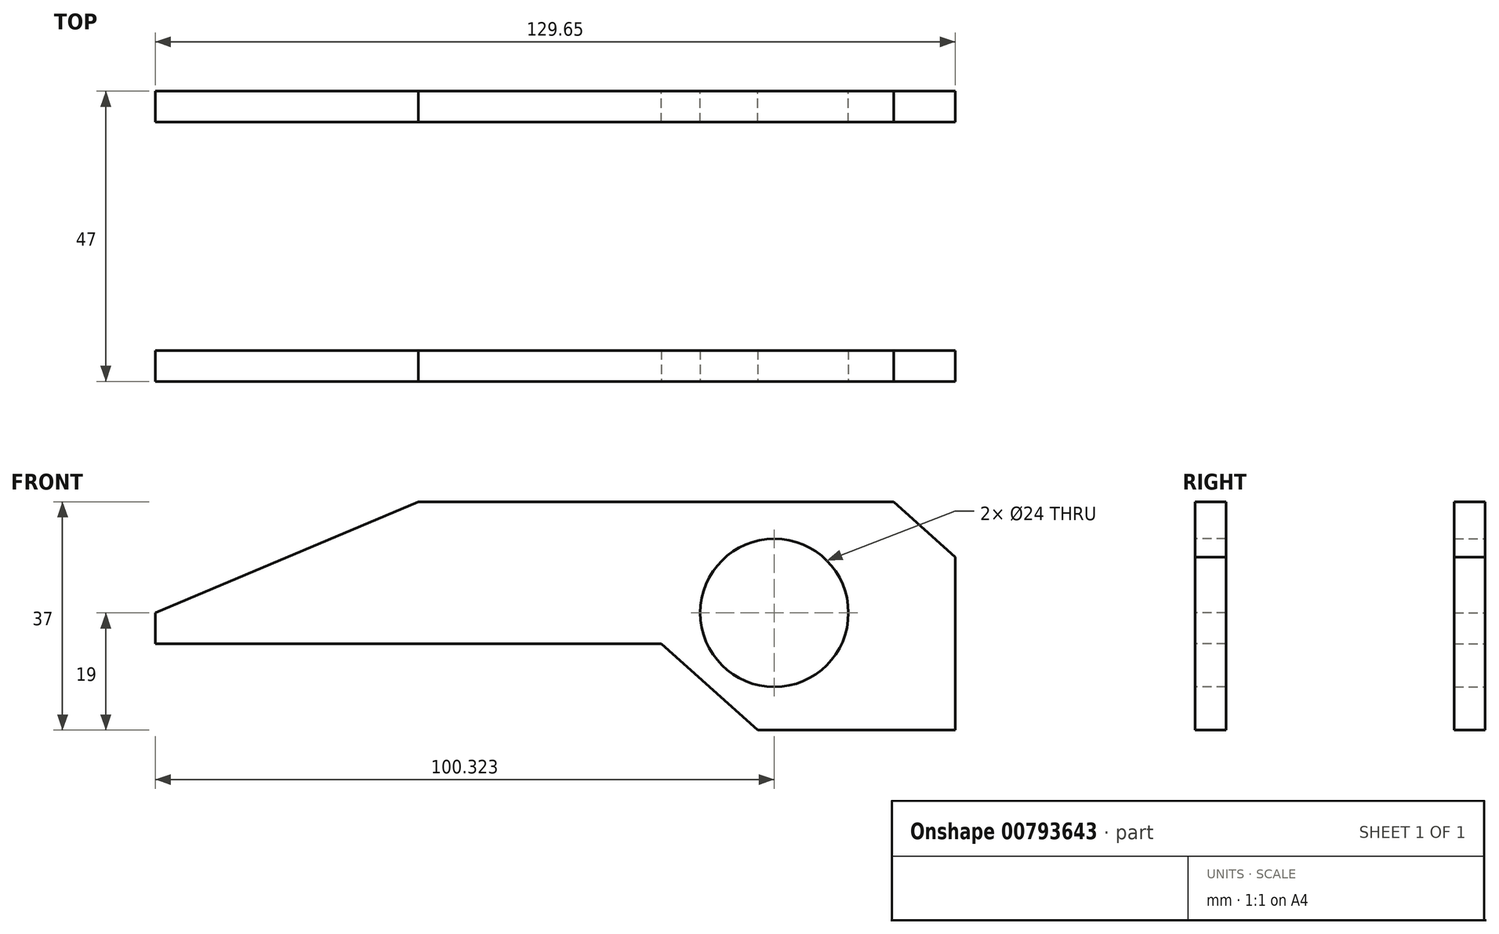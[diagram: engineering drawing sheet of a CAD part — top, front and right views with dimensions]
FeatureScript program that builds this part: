
annotation { "Feature Type Name" : "Feature", "Feature Type Description" : "" }
export const myFeature = defineFeature(function(context is Context, id is Id, definition is map)
    precondition{}
    {
        {
            var Q0;
            Q0=qCreatedBy(makeId("Front.planeOp"),FACE);
            var sketch = newSketch(context, id + "F0", { "sketchPlane" : qUnion([Q0])});
            skLineSegment(sketch, "E0", {"start": v(67.46, 14) * mm, "end": v(57.46, 23) * mm});
            skLineSegment(sketch, "E1", {"start": v(57.46, 23) * mm, "end": v(-19.54, 23) * mm});
            skLineSegment(sketch, "E2", {"start": v(-19.54, 23) * mm, "end": v(-62.2, 5) * mm});
            skLineSegment(sketch, "E3", {"start": v(-62.2, 5) * mm, "end": v(-62.2, 0) * mm});
            skLineSegment(sketch, "E4", {"start": v(-62.2, 0) * mm, "end": v(19.8, 0) * mm});
            skLineSegment(sketch, "E5", {"start": v(19.8, 0) * mm, "end": v(35.46, -14) * mm});
            skLineSegment(sketch, "E6", {"start": v(35.46, -14) * mm, "end": v(67.46, -14) * mm});
            skLineSegment(sketch, "E7", {"start": v(67.46, -14) * mm, "end": v(67.46, 14) * mm});
            skCircle(sketch, "E8", {"center": v(38.13, 5) * mm, "radius": 12 * mm});
            skSolve(sketch);
        }
        {
            var Q0;
            Q0 = qSketchRegion(id + "F0", true);
            extrude(context, id + "F1", {"entities" : qUnion([Q0]), "depth" : 5 * mm, "offsetDistance" : 25 * mm});
        }
        {
            var Q0;
            Q0=qCreatedBy(makeId("Front.planeOp"),FACE);
            cPlane(context, id + "F2", {"entities" : qUnion([Q0]), "cplaneType" : CPlaneType.OFFSET, "offset" : (47 / 2) * mm, "width" : 150 * mm, "height" : 150 * mm});
        }
        {
            var Q0;
            Q0=makeQuery(id+"F1.opExtrude","SWEPT_BODY",BODY,{"disambiguationData":[OSD([sQuery(id+"F0.wireOp",EDGE,"E0"),sQuery(id+"F0.wireOp",EDGE,"E1"),sQuery(id+"F0.wireOp",EDGE,"E2"),sQuery(id+"F0.wireOp",EDGE,"E3"),sQuery(id+"F0.wireOp",EDGE,"E4"),sQuery(id+"F0.wireOp",EDGE,"E5"),sQuery(id+"F0.wireOp",EDGE,"E6"),sQuery(id+"F0.wireOp",EDGE,"E7"),sQuery(id+"F0.wireOp",EDGE,"E8")])]});
            var Q1;
            Q1=qCreatedBy(id+"F2.planeOp",FACE);
            mirror(context, id + "F3", {"operationType" : NewBodyOperationType.ADD, "entities" : qUnion([Q0]), "mirrorPlane" : qUnion([Q1])});
        }
    });
